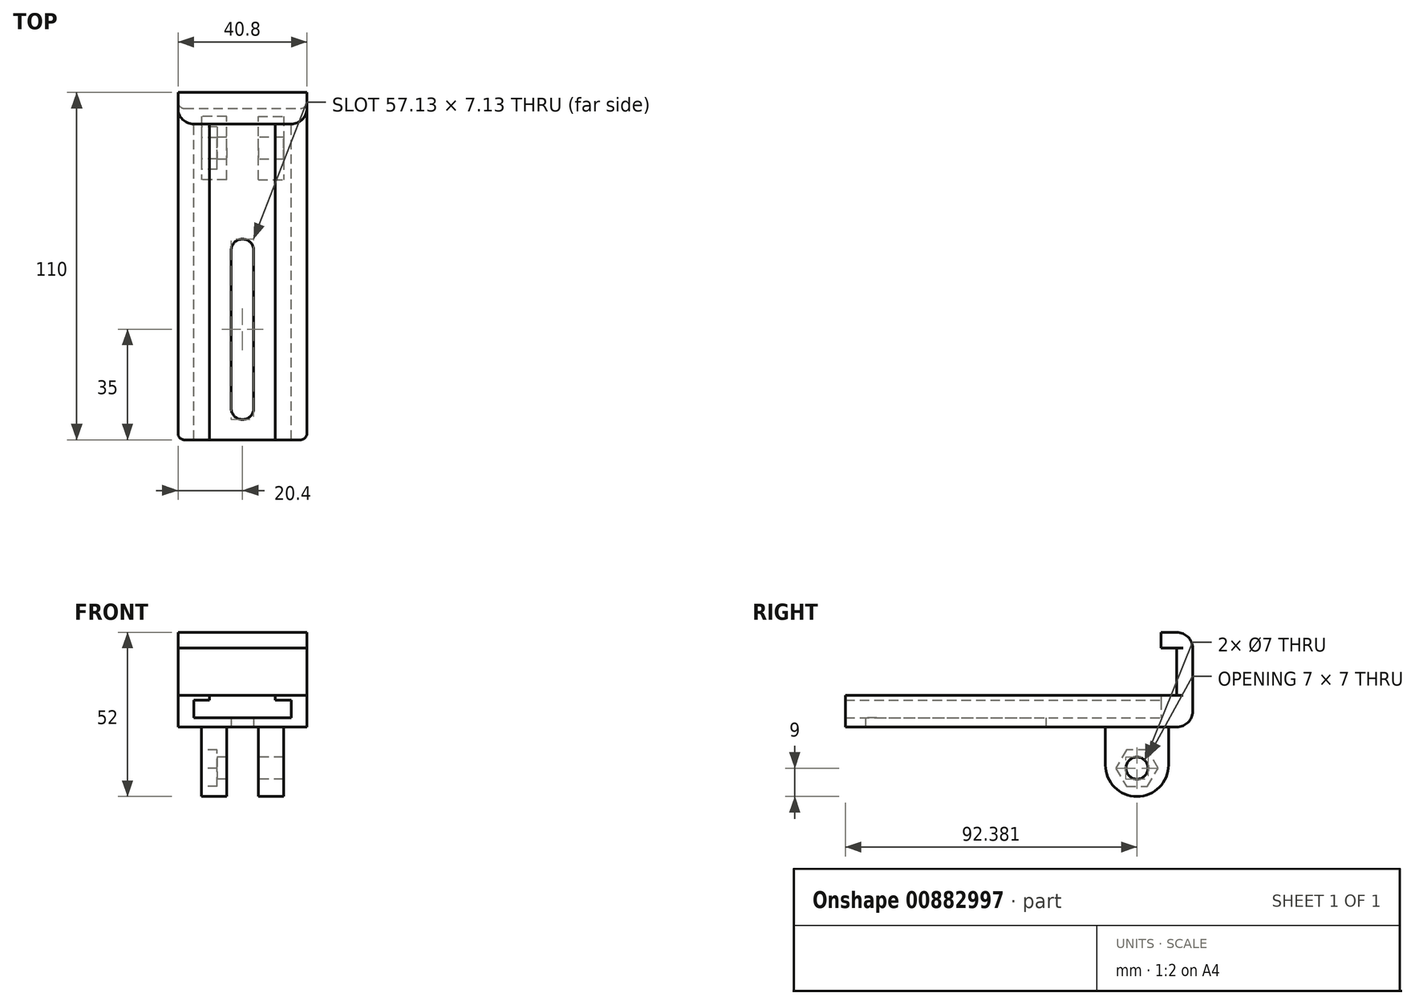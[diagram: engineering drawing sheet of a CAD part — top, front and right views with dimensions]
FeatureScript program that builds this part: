
annotation { "Feature Type Name" : "Feature", "Feature Type Description" : "" }
export const myFeature = defineFeature(function(context is Context, id is Id, definition is map)
    precondition{}
    {
        {
            var Q0;
            Q0=qCreatedBy(makeId("Top.planeOp"),FACE);
            var sketch = newSketch(context, id + "F0", { "sketchPlane" : qUnion([Q0])});
            skLineSegment(sketch, "E0.bottom", {"start": v(10.4, -50) * mm, "end": v(-10.4, -50) * mm});
            skLineSegment(sketch, "E0.top", {"start": v(10.4, 50) * mm, "end": v(-10.4, 50) * mm});
            skLineSegment(sketch, "E0.left", {"start": v(10.4, -50) * mm, "end": v(10.4, 50) * mm});
            skLineSegment(sketch, "E0.right", {"start": v(-10.4, -50) * mm, "end": v(-10.4, 50) * mm});
            skPoint(sketch, "E0.middle", {"position": v(0, 0) * mm});
            skLineSegment(sketch, "E1.bottom", {"start": v(-10.4, 50) * mm, "end": v(-20.4, 50) * mm});
            skLineSegment(sketch, "E1.top", {"start": v(-10.4, -50) * mm, "end": v(-20.4, -50) * mm});
            skLineSegment(sketch, "E1.left", {"start": v(-10.4, 50) * mm, "end": v(-10.4, -50) * mm});
            skLineSegment(sketch, "E1.right", {"start": v(-20.4, 50) * mm, "end": v(-20.4, -50) * mm});
            skLineSegment(sketch, "E2.bottom", {"start": v(10.4, 50) * mm, "end": v(20.4, 50) * mm});
            skLineSegment(sketch, "E2.top", {"start": v(10.4, -50) * mm, "end": v(20.4, -50) * mm});
            skLineSegment(sketch, "E2.left", {"start": v(10.4, 50) * mm, "end": v(10.4, -50) * mm});
            skLineSegment(sketch, "E2.right", {"start": v(20.4, 50) * mm, "end": v(20.4, -50) * mm});
            skLineSegment(sketch, "E3.left", {"start": v(3.57, -40) * mm, "end": v(3.57, 10) * mm});
            skLineSegment(sketch, "E4.bottom", {"start": v(-20.4, 50) * mm, "end": v(20.4, 50) * mm});
            skLineSegment(sketch, "E4.top", {"start": v(-20.4, 60) * mm, "end": v(20.4, 60) * mm});
            skLineSegment(sketch, "E4.left", {"start": v(-20.4, 50) * mm, "end": v(-20.4, 60) * mm});
            skLineSegment(sketch, "E4.right", {"start": v(20.4, 50) * mm, "end": v(20.4, 60) * mm});
            skLineSegment(sketch, "E5.left", {"start": v(-3.57, -40) * mm, "end": v(-3.57, 10) * mm});
            skArc(sketch, "E6", {"start": v(-3.57, 10) * mm, "mid": v(0, 13.57) * mm, "end": v(3.57, 10) * mm});
            skArc(sketch, "E7", {"start": v(3.57, -40) * mm, "mid": v(0, -43.57) * mm, "end": v(-3.57, -40) * mm});
            skSolve(sketch);
        }
        {
            var Q0;
            Q0=makeQuery(id+"F0.imprint","IMPRINT",FACE,{"disambiguationData":[TD([[makeQuery(id+"F0.imprint","IMPRINT",EDGE,{"derivedFrom":sQuery(id+"F0.wireOp",EDGE,"E0.right")}),1.0]])]});
            var Q1;
            Q1=makeQuery(id+"F0.imprint","IMPRINT",FACE,{"disambiguationData":[TD([[makeQuery(id+"F0.imprint","IMPRINT",EDGE,{"derivedFrom":sQuery(id+"F0.wireOp",EDGE,"E0.top")}),-1.0]])]});
            var Q2;
            Q2=makeQuery(id+"F0.imprint","IMPRINT",FACE,{"disambiguationData":[TD([[makeQuery(id+"F0.imprint","IMPRINT",EDGE,{"derivedFrom":sQuery(id+"F0.wireOp",EDGE,"E0.left")}),-1.0]])]});
            extrude(context, id + "F1", {"entities" : qUnion([Q0, Q1, Q2]), "depth" : 10 * mm, "offsetDistance" : 25 * mm});
        }
        {
            var Q0;
            Q0=makeQuery(id+"F0.imprint","IMPRINT",FACE,{"disambiguationData":[TD([[makeQuery(id+"F0.imprint","IMPRINT",EDGE,{"derivedFrom":sQuery(id+"F0.wireOp",EDGE,"E0.bottom")}),-1.0]])]});
            extrude(context, id + "F2", {"entities" : qUnion([Q0]), "operationType" : NewBodyOperationType.ADD, "depth" : 5 * mm, "offsetDistance" : 25 * mm});
        }
        {
            var Q0;
            Q0=makeQuery(id+"F1.opExtrude","CAP_FACE",FACE,{"disambiguationData":[OSD([sQuery(id+"F0.wireOp",EDGE,"E0.top"),sQuery(id+"F0.wireOp",EDGE,"E0.left"),sQuery(id+"F0.wireOp",EDGE,"E0.right"),sQuery(id+"F0.wireOp",EDGE,"E1.top"),sQuery(id+"F0.wireOp",EDGE,"E1.right"),sQuery(id+"F0.wireOp",EDGE,"E2.top"),sQuery(id+"F0.wireOp",EDGE,"E2.right"),sQuery(id+"F0.wireOp",EDGE,"E4.top"),sQuery(id+"F0.wireOp",EDGE,"E4.left"),sQuery(id+"F0.wireOp",EDGE,"E4.right")])],"isStart":false});
            var sketch = newSketch(context, id + "F3", { "sketchPlane" : qUnion([Q0])});
            skLineSegment(sketch, "E8.bottom", {"start": v(-20.4, 60) * mm, "end": v(20.4, 60) * mm});
            skLineSegment(sketch, "E8.top", {"start": v(-20.4, 55) * mm, "end": v(20.4, 55) * mm});
            skLineSegment(sketch, "E8.left", {"start": v(-20.4, 60) * mm, "end": v(-20.4, 55) * mm});
            skLineSegment(sketch, "E8.right", {"start": v(20.4, 60) * mm, "end": v(20.4, 55) * mm});
            skSolve(sketch);
        }
        {
            var Q0;
            Q0 = qSketchRegion(id + "F3", true);
            extrude(context, id + "F4", {"entities" : qUnion([Q0]), "operationType" : NewBodyOperationType.ADD, "depth" : 15 * mm, "offsetDistance" : 25 * mm});
        }
        {
            var Q0;
            Q0=makeQuery(id+"F4.opExtrude","CAP_FACE",FACE,{"disambiguationData":[OSD([sQuery(id+"F3.wireOp",EDGE,"E8.bottom"),sQuery(id+"F3.wireOp",EDGE,"E8.top"),sQuery(id+"F3.wireOp",EDGE,"E8.left"),sQuery(id+"F3.wireOp",EDGE,"E8.right")])],"isStart":false});
            var sketch = newSketch(context, id + "F5", { "sketchPlane" : qUnion([Q0])});
            skLineSegment(sketch, "E9.bottom", {"start": v(-20.4, 60) * mm, "end": v(20.4, 60) * mm});
            skLineSegment(sketch, "E9.top", {"start": v(-20.4, 50) * mm, "end": v(20.4, 50) * mm});
            skLineSegment(sketch, "E9.left", {"start": v(-20.4, 60) * mm, "end": v(-20.4, 50) * mm});
            skLineSegment(sketch, "E9.right", {"start": v(20.4, 60) * mm, "end": v(20.4, 50) * mm});
            skSolve(sketch);
        }
        {
            var Q0;
            Q0 = qSketchRegion(id + "F5", true);
            extrude(context, id + "F6", {"entities" : qUnion([Q0]), "operationType" : NewBodyOperationType.ADD, "depth" : 5 * mm, "offsetDistance" : 25 * mm});
        }
        {
            var Q0;
            {var subQ0=sQuery(id+"F0.wireOp",EDGE,"E0.right");var subQ1=sQuery(id+"F0.wireOp",EDGE,"E0.left");var subQ2=sQuery(id+"F0.wireOp",EDGE,"E0.top");Q0=makeQuery(id+"F2.boolean.opBoolean","MERGE",FACE,{"derivedFrom":[makeQuery(id+"F1.opExtrude","CAP_FACE",FACE,{"disambiguationData":[OSD([subQ2,subQ1,subQ0,sQuery(id+"F0.wireOp",EDGE,"E1.top"),sQuery(id+"F0.wireOp",EDGE,"E1.right"),sQuery(id+"F0.wireOp",EDGE,"E2.top"),sQuery(id+"F0.wireOp",EDGE,"E2.right"),sQuery(id+"F0.wireOp",EDGE,"E4.top"),sQuery(id+"F0.wireOp",EDGE,"E4.left"),sQuery(id+"F0.wireOp",EDGE,"E4.right")])],"isStart":true}),makeQuery(id+"F2.opExtrude","CAP_FACE",FACE,{"disambiguationData":[OSD([sQuery(id+"F0.wireOp",EDGE,"E0.bottom"),subQ2,subQ1,subQ0,sQuery(id+"F0.wireOp",EDGE,"E3.left"),sQuery(id+"F0.wireOp",EDGE,"E5.left"),sQuery(id+"F0.wireOp",EDGE,"E6"),sQuery(id+"F0.wireOp",EDGE,"E7")])],"isStart":true})]});}
            var sketch = newSketch(context, id + "F7", { "sketchPlane" : qUnion([Q0])});
            skLineSegment(sketch, "E10.left", {"start": v(-5, -32.38) * mm, "end": v(-5, -52.38) * mm});
            skLineSegment(sketch, "E10.right", {"start": v(5, -32.38) * mm, "end": v(5, -52.38) * mm});
            skPoint(sketch, "E10.middle", {"position": v(0, -42.38) * mm});
            skLineSegment(sketch, "E11.bottom", {"start": v(5, -52.38) * mm, "end": v(13, -52.38) * mm});
            skLineSegment(sketch, "E11.top", {"start": v(5, -32.38) * mm, "end": v(13, -32.38) * mm});
            skLineSegment(sketch, "E11.left", {"start": v(5, -52.38) * mm, "end": v(5, -32.38) * mm});
            skLineSegment(sketch, "E11.right", {"start": v(13, -52.38) * mm, "end": v(13, -32.38) * mm});
            skLineSegment(sketch, "E12.bottom", {"start": v(-5, -52.38) * mm, "end": v(-13, -52.38) * mm});
            skLineSegment(sketch, "E12.top", {"start": v(-5, -32.38) * mm, "end": v(-13, -32.38) * mm});
            skLineSegment(sketch, "E12.left", {"start": v(-5, -52.38) * mm, "end": v(-5, -32.38) * mm});
            skLineSegment(sketch, "E12.right", {"start": v(-13, -52.38) * mm, "end": v(-13, -32.38) * mm});
            skSolve(sketch);
        }
        {
            var Q0;
            Q0=makeQuery(id+"F7.imprint","IMPRINT",FACE,{"disambiguationData":[TD([[makeQuery(id+"F7.imprint","IMPRINT",EDGE,{"derivedFrom":sQuery(id+"F7.wireOp",EDGE,"E11.bottom")}),1.0]])]});
            var Q1;
            Q1=makeQuery(id+"F7.imprint","IMPRINT",FACE,{"disambiguationData":[TD([[makeQuery(id+"F7.imprint","IMPRINT",EDGE,{"derivedFrom":sQuery(id+"F7.wireOp",EDGE,"E12.bottom")}),-1.0]])]});
            extrude(context, id + "F8", {"entities" : qUnion([Q0, Q1]), "operationType" : NewBodyOperationType.ADD, "depth" : 22 * mm, "offsetDistance" : 25 * mm});
        }
        {
            var Q0;
            Q0=makeQuery(id+"F8.opExtrude","SWEPT_FACE",FACE,{"disambiguationData":[OSD([sQuery(id+"F7.wireOp",EDGE,"E12.right")])]});
            var sketch = newSketch(context, id + "F9", { "sketchPlane" : qUnion([Q0])});
            skCircle(sketch, "E13", {"center": v(-42.38, -13) * mm, "radius": 3.5 * mm});
            skCircle(sketch, "E14.cCircle", {"center": v(-42.38, -13) * mm, "radius": 5.8 * mm, "construction": true});
            skLineSegment(sketch, "E14.0", {"start": v(-45.73, -7.2) * mm, "end": v(-39.03, -7.2) * mm});
            skLineSegment(sketch, "E14.1", {"start": v(-39.03, -7.2) * mm, "end": v(-35.68, -13) * mm});
            skLineSegment(sketch, "E14.2", {"start": v(-35.68, -13) * mm, "end": v(-39.03, -18.8) * mm});
            skLineSegment(sketch, "E14.3", {"start": v(-39.03, -18.8) * mm, "end": v(-45.73, -18.8) * mm});
            skLineSegment(sketch, "E14.4", {"start": v(-45.73, -18.8) * mm, "end": v(-49.08, -13) * mm});
            skLineSegment(sketch, "E14.5", {"start": v(-49.08, -13) * mm, "end": v(-45.73, -7.2) * mm});
            skPoint(sketch, "E14.0.midPoint", {"position": v(-42.38, -7.2) * mm});
            skSolve(sketch);
        }
        {
            var Q0;
            Q0=makeQuery(id+"F9.imprint","IMPRINT",FACE,{"disambiguationData":[TD([[makeQuery(id+"F9.imprint","IMPRINT",EDGE,{"derivedFrom":sQuery(id+"F9.wireOp",EDGE,"E13")}),1.0]])]});
            extrude(context, id + "F10", {"entities" : qUnion([Q0]), "operationType" : NewBodyOperationType.REMOVE, "endBound" : BoundingType.THROUGH_ALL, "oppositeDirection" : true, "depth" : 25 * mm, "offsetDistance" : 25 * mm});
        }
        {
            var Q0;
            Q0 = qSketchRegion(id + "F9", true);
            extrude(context, id + "F11", {"entities" : qUnion([Q0]), "operationType" : NewBodyOperationType.REMOVE, "oppositeDirection" : true, "depth" : 5 * mm, "offsetDistance" : 25 * mm});
        }
        {
            var Q0;
            Q0=makeQuery(id+"F8.opExtrude","CAP_EDGE",EDGE,{"disambiguationData":[OSD([sQuery(id+"F7.wireOp",EDGE,"E12.bottom")])],"isStart":false});
            var Q1;
            Q1=makeQuery(id+"F8.opExtrude","CAP_EDGE",EDGE,{"disambiguationData":[OSD([sQuery(id+"F7.wireOp",EDGE,"E11.bottom")])],"isStart":false});
            var Q2;
            Q2=makeQuery(id+"F8.opExtrude","CAP_EDGE",EDGE,{"disambiguationData":[OSD([sQuery(id+"F7.wireOp",EDGE,"E11.top")])],"isStart":false});
            var Q3;
            Q3=makeQuery(id+"F8.opExtrude","CAP_EDGE",EDGE,{"disambiguationData":[OSD([sQuery(id+"F7.wireOp",EDGE,"E12.top")])],"isStart":false});
            fillet(context, id + "F12", {"entities" : qUnion([Q0, Q1, Q2, Q3]), "radius" : 10 * mm, "tangentPropagation" : true, "allowEdgeOverflow" : false});
        }
        {
            var Q0;
            Q0=makeQuery(id+"F6.opExtrude","SWEPT_EDGE",EDGE,{"disambiguationData":[OSD([sQuery(id+"F5.wireOp",EDGE,"E9.top"),sQuery(id+"F5.wireOp",EDGE,"E9.left")])]});
            var Q1;
            Q1=makeQuery(id+"F6.opExtrude","SWEPT_EDGE",EDGE,{"disambiguationData":[OSD([sQuery(id+"F5.wireOp",EDGE,"E9.top"),sQuery(id+"F5.wireOp",EDGE,"E9.right")])]});
            var Q2;
            Q2=makeQuery(id+"F6.opExtrude","CAP_EDGE",EDGE,{"disambiguationData":[OSD([sQuery(id+"F5.wireOp",EDGE,"E9.bottom")])],"isStart":false});
            var Q3;
            Q3=makeQuery(id+"F1.opExtrude","CAP_EDGE",EDGE,{"disambiguationData":[OSD([sQuery(id+"F0.wireOp",EDGE,"E4.top")])],"isStart":true});
            fillet(context, id + "F13", {"entities" : qUnion([Q0, Q1, Q2, Q3]), "radius" : 5 * mm, "tangentPropagation" : true, "allowEdgeOverflow" : false});
        }
        {
            var Q0;
            Q0=makeQuery(id+"F4.opExtrude","SWEPT_EDGE",EDGE,{"disambiguationData":[OSD([sQuery(id+"F0.wireOp",EDGE,"E1.right"),sQuery(id+"F0.wireOp",EDGE,"E4.left"),sQuery(id+"F3.wireOp",EDGE,"E8.top"),sQuery(id+"F3.wireOp",EDGE,"E8.left")])]});
            var Q1;
            Q1=makeQuery(id+"F4.opExtrude","SWEPT_EDGE",EDGE,{"disambiguationData":[OSD([sQuery(id+"F0.wireOp",EDGE,"E2.right"),sQuery(id+"F0.wireOp",EDGE,"E4.right"),sQuery(id+"F3.wireOp",EDGE,"E8.top"),sQuery(id+"F3.wireOp",EDGE,"E8.right")])]});
            var Q2;
            Q2=makeQuery(id+"F1.opExtrude","SWEPT_EDGE",EDGE,{"disambiguationData":[OSD([sQuery(id+"F0.wireOp",EDGE,"E1.top"),sQuery(id+"F0.wireOp",EDGE,"E1.right")])]});
            var Q3;
            Q3=makeQuery(id+"F1.opExtrude","SWEPT_EDGE",EDGE,{"disambiguationData":[OSD([sQuery(id+"F0.wireOp",EDGE,"E2.top"),sQuery(id+"F0.wireOp",EDGE,"E2.right")])]});
            fillet(context, id + "F14", {"entities" : qUnion([Q0, Q1, Q2, Q3]), "radius" : 2 * mm, "tangentPropagation" : true, "allowEdgeOverflow" : false});
        }
        {
            var Q0;
            Q0=makeQuery(id+"F1.opExtrude","SWEPT_FACE",FACE,{"disambiguationData":[OSD([sQuery(id+"F0.wireOp",EDGE,"E0.right")])]});
            var sketch = newSketch(context, id + "F15", { "sketchPlane" : qUnion([Q0])});
            skLineSegment(sketch, "E15.bottom", {"start": v(-50, 5) * mm, "end": v(50, 5) * mm});
            skLineSegment(sketch, "E15.top", {"start": v(-50, 8.5) * mm, "end": v(50, 8.5) * mm});
            skLineSegment(sketch, "E15.left", {"start": v(-50, 5) * mm, "end": v(-50, 8.5) * mm});
            skLineSegment(sketch, "E15.right", {"start": v(50, 5) * mm, "end": v(50, 8.5) * mm});
            skSolve(sketch);
        }
        {
            var Q0;
            Q0 = qSketchRegion(id + "F15", true);
            extrude(context, id + "F16", {"entities" : qUnion([Q0]), "operationType" : NewBodyOperationType.REMOVE, "oppositeDirection" : true, "depth" : 5 * mm, "offsetDistance" : 25 * mm});
        }
        {
            var Q0;
            Q0=makeQuery(id+"F1.opExtrude","SWEPT_FACE",FACE,{"disambiguationData":[OSD([sQuery(id+"F0.wireOp",EDGE,"E0.left")])]});
            var sketch = newSketch(context, id + "F17", { "sketchPlane" : qUnion([Q0])});
            skLineSegment(sketch, "E16.bottom", {"start": v(50, 5) * mm, "end": v(-50, 5) * mm});
            skLineSegment(sketch, "E16.top", {"start": v(50, 8.5) * mm, "end": v(-50, 8.5) * mm});
            skLineSegment(sketch, "E16.left", {"start": v(50, 5) * mm, "end": v(50, 8.5) * mm});
            skLineSegment(sketch, "E16.right", {"start": v(-50, 5) * mm, "end": v(-50, 8.5) * mm});
            skSolve(sketch);
        }
        {
            var Q0;
            Q0 = qSketchRegion(id + "F17", true);
            extrude(context, id + "F18", {"entities" : qUnion([Q0]), "operationType" : NewBodyOperationType.REMOVE, "oppositeDirection" : true, "depth" : 5 * mm, "offsetDistance" : 25 * mm});
        }
        {
            var Q0;
            Q0=makeQuery(id+"F18.boolean.opBoolean","MERGE",FACE,{"derivedFrom":[makeQuery(id+"F16.boolean.opBoolean","MERGE",FACE,{"derivedFrom":[makeQuery(id+"F2.opExtrude","CAP_FACE",FACE,{"disambiguationData":[OSD([sQuery(id+"F0.wireOp",EDGE,"E0.bottom"),sQuery(id+"F0.wireOp",EDGE,"E0.top"),sQuery(id+"F0.wireOp",EDGE,"E0.left"),sQuery(id+"F0.wireOp",EDGE,"E0.right"),sQuery(id+"F0.wireOp",EDGE,"E3.left"),sQuery(id+"F0.wireOp",EDGE,"E5.left"),sQuery(id+"F0.wireOp",EDGE,"E6"),sQuery(id+"F0.wireOp",EDGE,"E7")])],"isStart":false})],"fromTools":[makeQuery(id+"F16.opExtrude","SWEPT_FACE",FACE,{"disambiguationData":[OSD([sQuery(id+"F15.wireOp",EDGE,"E15.bottom")])]})]})],"fromTools":[makeQuery(id+"F18.opExtrude","SWEPT_FACE",FACE,{"disambiguationData":[OSD([sQuery(id+"F17.wireOp",EDGE,"E16.bottom")])]})]});
            extrude(context, id + "F19", {"entities" : qUnion([Q0]), "operationType" : NewBodyOperationType.REMOVE, "oppositeDirection" : true, "depth" : 2 * mm, "offsetDistance" : 25 * mm});
        }
    });
